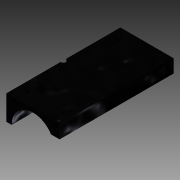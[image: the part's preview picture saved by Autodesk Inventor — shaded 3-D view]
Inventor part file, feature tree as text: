
AUTODESK INVENTOR PART (.ipt)
format: ipt  version: 2015 (Build 190159000, 159)  size: 193,536 bytes
history: native  units: mm
features: other x4, extrude x4, sketch x4, projected_geometry x3
ambient origin geometry x8: Origin, YZ Plane, XZ Plane, XY Plane, X Axis, Y Axis, Z Axis, Center Point
bodies: Solid1 (feature_tree)
feature tree (15):
  other  "motor mount.ipt"
  extrude  "Extrusion1"  Depth=10.0mm
  extrude  "Extrusion2"  Depth=60.0mm
  extrude  "Extrusion4"  Depth=2.3mm
  extrude  "Extrusion5"  Depth=3.0mm
  other  "TaggingFeature1"
  sketch  "Sketch2"  dims[d1=10.0mm d2=11.25mm]
  sketch  "Sketch3"  dims[d3=60.0mm d4=0.0mm d5=2.3mm]
  projected_geometry  "Projected Loop1"
  sketch  "Sketch4"  dims[d6=2.3mm d7=2.3mm]
  projected_geometry  "Projected Loop2"
  sketch  "Sketch5"  dims[d8=2.3mm d9=4.5mm d10=4.5mm d11=6.0mm d12=6.0mm d13=60.0mm d14=0.0mm d15=19.0mm d16=48.0mm d19=6.0mm d20=0.0mm d21=3.0mm d22=100.0mm d23=0.0mm]
  projected_geometry  "Projected Loop3"
  other  "Solid1::motor mount.ipt"
  other  "Srf1"
